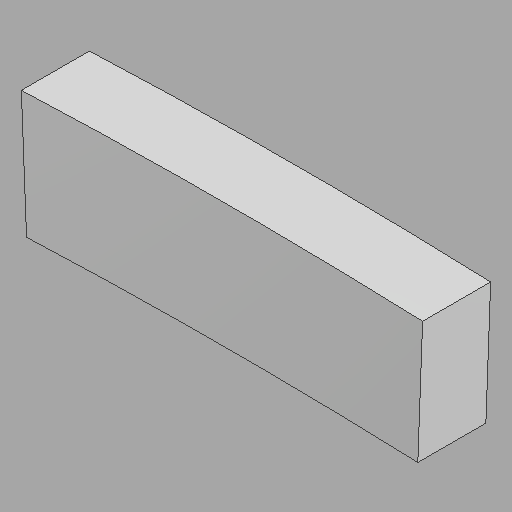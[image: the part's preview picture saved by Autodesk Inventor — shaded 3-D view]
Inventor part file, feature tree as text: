
AUTODESK INVENTOR PART (.ipt)
format: ipt  version: 2022.1 (Build 261234020, 234B)  size: 88,576 bytes
history: imported  units: in
note: dims shown in document units (in); Inventor stores cm internally (conversion verified against a paired STEP export)
features: imported_body x1
ambient origin geometry x8: Origin, YZ Plane, XZ Plane, XY Plane, X Axis, Y Axis, Z Axis, Center Point
bodies: Solid1 (imported_parasolid)
feature tree (1):
  imported_body  NMx_Import_Brep_tag  [imported B-rep: ~6 faces, bbox_mm=[898.52895, 280.549482, 152.4]]
